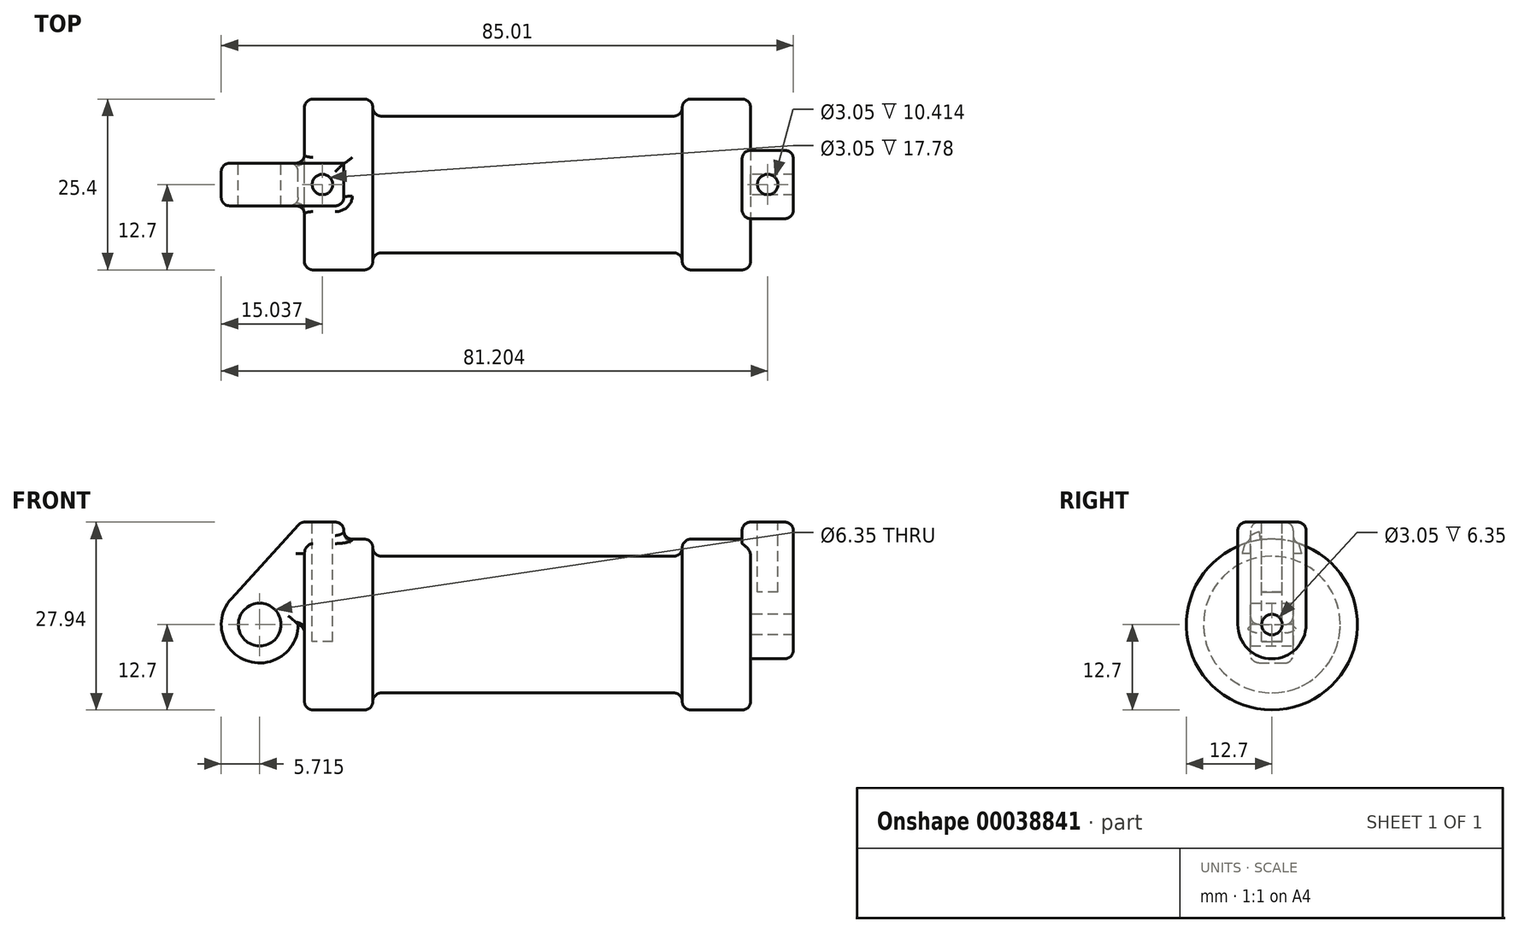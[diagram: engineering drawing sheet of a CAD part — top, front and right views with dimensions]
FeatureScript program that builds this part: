
annotation { "Feature Type Name" : "Feature", "Feature Type Description" : "" }
export const myFeature = defineFeature(function(context is Context, id is Id, definition is map)
    precondition{}
    {
        {
            var Q0;
            Q0=qCreatedBy(makeId("Front.planeOp"),FACE);
            var sketch = newSketch(context, id + "F0", { "sketchPlane" : qUnion([Q0])});
            skLineSegment(sketch, "E0", {"start": v(0, 0) * mm, "end": v(0, 12.7) * mm});
            skLineSegment(sketch, "E1", {"start": v(0, 12.7) * mm, "end": v(10.16, 12.7) * mm});
            skLineSegment(sketch, "E2", {"start": v(10.16, 12.7) * mm, "end": v(10.16, 10.16) * mm});
            skLineSegment(sketch, "E3", {"start": v(10.16, 10.16) * mm, "end": v(56.13, 10.16) * mm});
            skLineSegment(sketch, "E4", {"start": v(56.13, 10.16) * mm, "end": v(56.13, 12.7) * mm});
            skLineSegment(sketch, "E5", {"start": v(56.13, 12.7) * mm, "end": v(66.3, 12.7) * mm});
            skLineSegment(sketch, "E6", {"start": v(66.3, 12.7) * mm, "end": v(66.3, 0) * mm});
            skLineSegment(sketch, "E7", {"start": v(66.3, 0) * mm, "end": v(0, 0) * mm});
            skLineSegment(sketch, "E8", {"start": v(5.84, 15.24) * mm, "end": v(-0.5, 15.24) * mm});
            skLineSegment(sketch, "E9", {"start": v(-0.5, 15.24) * mm, "end": v(-10.88, 3.85) * mm});
            skLineSegment(sketch, "E10", {"start": v(0, 0) * mm, "end": v(-6.65, 0) * mm});
            skCircle(sketch, "E11", {"center": v(-6.65, 0) * mm, "radius": 5.72 * mm});
            skCircle(sketch, "E12", {"center": v(-6.65, 0) * mm, "radius": 3.18 * mm});
            skLineSegment(sketch, "E13", {"start": v(5.84, 15.24) * mm, "end": v(5.84, -9.4) * mm});
            skLineSegment(sketch, "E14", {"start": v(5.84, -9.4) * mm, "end": v(-8.18, -5.5) * mm});
            skSolve(sketch);
        }
        {
            var Q0;
            {var subQ6=sQuery(id+"F0.wireOp",EDGE,"E2");Q0=makeQuery(id+"F0.imprint","IMPRINT",FACE,{"disambiguationData":[TD([[makeQuery(id+"F0.imprint","IMPRINT",EDGE,{"derivedFrom":subQ6}),-1.0]])]});}
            var Q1;
            {var subQ5=sQuery(id+"F0.wireOp",EDGE,"E0");Q1=makeQuery(id+"F0.imprint","IMPRINT",FACE,{"disambiguationData":[TD([[makeQuery(id+"F0.imprint","IMPRINT",EDGE,{"derivedFrom":subQ5}),-1.0]])]});}
            var Q2;
            Q2=sQuery(id+"F0.wireOp",EDGE,"E7");
            revolve(context, id + "F1", {"entities" : qUnion([Q0, Q1]), "axis" : qUnion([Q2]), "revolveType" : RevolveType.FULL});
        }
        {
            var Q0;
            {var subQ8=sQuery(id+"F0.wireOp",EDGE,"E0");Q0=makeQuery(id+"F0.imprint","IMPRINT",FACE,{"disambiguationData":[TD([[makeQuery(id+"F0.imprint","IMPRINT",EDGE,{"derivedFrom":subQ8}),1.0]])]});}
            var Q1;
            {var subQ0=sQuery(id+"F0.wireOp",EDGE,"E12");Q1=makeQuery(id+"F0.imprint","IMPRINT",FACE,{"disambiguationData":[TD([[makeQuery(id+"F0.imprint","IMPRINT",EDGE,{"derivedFrom":subQ0}),-1.0]])]});}
            var Q2;
            {var subQ5=sQuery(id+"F0.wireOp",EDGE,"E0");Q2=makeQuery(id+"F0.imprint","IMPRINT",FACE,{"disambiguationData":[TD([[makeQuery(id+"F0.imprint","IMPRINT",EDGE,{"derivedFrom":subQ5}),-1.0]])]});}
            extrude(context, id + "F2", {"entities" : qUnion([Q0, Q1, Q2]), "operationType" : NewBodyOperationType.ADD, "endBound" : BoundingType.SYMMETRIC, "depth" : 6.35 * mm});
        }
        {
            var Q0;
            Q0=makeQuery(id+"F1.opRevolve","SWEPT_FACE",FACE,{"disambiguationData":[OSD([sQuery(id+"F0.wireOp",EDGE,"E6")])]});
            var sketch = newSketch(context, id + "F3", { "sketchPlane" : qUnion([Q0])});
            skCircle(sketch, "E15", {"center": v(0, 0) * mm, "radius": 5.08 * mm});
            skCircle(sketch, "E16", {"center": v(0, 0) * mm, "radius": 1.52 * mm});
            skLineSegment(sketch, "E17", {"start": v(-5.08, 0) * mm, "end": v(-5.08, 15.24) * mm});
            skLineSegment(sketch, "E18", {"start": v(-5.08, 15.24) * mm, "end": v(5.08, 15.24) * mm});
            skLineSegment(sketch, "E19", {"start": v(5.08, 0) * mm, "end": v(5.08, 15.28) * mm});
            skSolve(sketch);
        }
        {
            var Q0;
            Q0=makeQuery(id+"F3.imprint","IMPRINT",FACE,{"disambiguationData":[TD([[makeQuery(id+"F3.imprint","IMPRINT",EDGE,{"derivedFrom":sQuery(id+"F3.wireOp",EDGE,"E16")}),-1.0]])]});
            var Q1;
            {var subQ5=sQuery(id+"F3.wireOp",EDGE,"E18");Q1=makeQuery(id+"F3.imprint","IMPRINT",FACE,{"disambiguationData":[TD([[makeQuery(id+"F3.imprint","IMPRINT",EDGE,{"derivedFrom":subQ5}),-1.0]])]});}
            var Q2;
            {var subQ3=sQuery(id+"F3.wireOp",EDGE,"E15");var subQ5=sQuery(id+"F3.wireOp",EDGE,"E17");var subQ7=makeQuery(id+"F3.imprint","INTERSECT",VERTEX,{"derivedFrom":[subQ3,subQ5]});Q2=makeQuery(id+"F3.imprint","IMPRINT",FACE,{"disambiguationData":[TD([[makeQuery(id+"F3.imprint","IMPRINT",EDGE,{"disambiguationData":[TD([[subQ7,1.0]])],"derivedFrom":subQ3}),-1.0]])]});}
            extrude(context, id + "F4", {"entities" : qUnion([Q0, Q1, Q2]), "operationType" : NewBodyOperationType.ADD, "depth" : 6.35 * mm});
        }
        {
            var Q0;
            Q0=makeQuery(id+"F4.opExtrude","CAP_FACE",FACE,{"disambiguationData":[OSD([sQuery(id+"F3.wireOp",EDGE,"E15"),sQuery(id+"F3.wireOp",EDGE,"E16"),sQuery(id+"F3.wireOp",EDGE,"E17"),sQuery(id+"F3.wireOp",EDGE,"E18"),sQuery(id+"F3.wireOp",EDGE,"E19")])],"isStart":true});
            extrude(context, id + "F5", {"entities" : qUnion([Q0]), "operationType" : NewBodyOperationType.ADD, "depth" : 1.27 * mm});
        }
        {
            var Q0;
            {var subQ0=sQuery(id+"F3.wireOp",EDGE,"E18");Q0=makeQuery(id+"F5.boolean.opBoolean","MERGE",FACE,{"derivedFrom":[makeQuery(id+"F4.opExtrude","SWEPT_FACE",FACE,{"disambiguationData":[OSD([subQ0])]}),makeQuery(id+"F5.opExtrude","SWEPT_FACE",FACE,{"disambiguationData":[OSD([subQ0])]})]});}
            var sketch = newSketch(context, id + "F6", { "sketchPlane" : qUnion([Q0])});
            skLineSegment(sketch, "E20", {"start": v(68.83, 5.08) * mm, "end": v(68.83, -5.08) * mm, "construction": true});
            skCircle(sketch, "E21", {"center": v(68.83, 0) * mm, "radius": 1.52 * mm});
            skSolve(sketch);
        }
        {
            var Q0;
            Q0=makeQuery(id+"F6.imprint","IMPRINT",FACE,{"disambiguationData":[TD([[makeQuery(id+"F6.imprint","IMPRINT",EDGE,{"derivedFrom":sQuery(id+"F6.wireOp",EDGE,"E21")}),1.0]])]});
            extrude(context, id + "F7", {"entities" : qUnion([Q0]), "operationType" : NewBodyOperationType.REMOVE, "oppositeDirection" : true, "depth" : 10.4 * mm});
        }
        {
            var Q0;
            Q0=makeQuery(id+"F2.opExtrude","SWEPT_FACE",FACE,{"disambiguationData":[OSD([sQuery(id+"F0.wireOp",EDGE,"E8")])]});
            var sketch = newSketch(context, id + "F8", { "sketchPlane" : qUnion([Q0])});
            skLineSegment(sketch, "E22", {"start": v(2.67, 3.18) * mm, "end": v(2.67, -3.18) * mm, "construction": true});
            skCircle(sketch, "E23", {"center": v(2.67, 0) * mm, "radius": 1.52 * mm});
            skSolve(sketch);
        }
        {
            var Q0;
            Q0=makeQuery(id+"F8.imprint","IMPRINT",FACE,{"disambiguationData":[TD([[makeQuery(id+"F8.imprint","IMPRINT",EDGE,{"derivedFrom":sQuery(id+"F8.wireOp",EDGE,"E23")}),1.0]])]});
            var Q1;
            Q1=sQuery(id+"F8.wireOp",EDGE,"E23");
            extrude(context, id + "F9", {"entities" : qUnion([Q0]), "operationType" : NewBodyOperationType.REMOVE, "surfaceEntities" : qUnion([Q1]), "oppositeDirection" : true, "depth" : 17.78 * mm});
        }
        {
            var Q0;
            Q0=makeQuery(id+"F1.opRevolve","SWEPT_EDGE",EDGE,{"disambiguationData":[OSD([sQuery(id+"F0.wireOp",EDGE,"E1"),sQuery(id+"F0.wireOp",EDGE,"E2")])]});
            var Q1;
            Q1=makeQuery(id+"F1.opRevolve","SWEPT_EDGE",EDGE,{"disambiguationData":[OSD([sQuery(id+"F0.wireOp",EDGE,"E0"),sQuery(id+"F0.wireOp",EDGE,"E1")])]});
            var Q2;
            Q2=makeQuery(id+"F1.opRevolve","SWEPT_EDGE",EDGE,{"disambiguationData":[OSD([sQuery(id+"F0.wireOp",EDGE,"E3"),sQuery(id+"F0.wireOp",EDGE,"E4")])]});
            var Q3;
            Q3=makeQuery(id+"F1.opRevolve","SWEPT_EDGE",EDGE,{"disambiguationData":[OSD([sQuery(id+"F0.wireOp",EDGE,"E4"),sQuery(id+"F0.wireOp",EDGE,"E5")])]});
            var Q4;
            Q4=makeQuery(id+"F4.boolean.opBoolean","SPLIT",EDGE,{"disambiguationData":[OD(1.0)],"derivedFrom":makeQuery(id+"F1.opRevolve","SWEPT_EDGE",EDGE,{"disambiguationData":[OSD([sQuery(id+"F0.wireOp",EDGE,"E5"),sQuery(id+"F0.wireOp",EDGE,"E6")])]})});
            fillet(context, id + "F10", {"entities" : qUnion([Q0, Q1, Q2, Q3, Q4]), "radius" : 1.27 * mm, "tangentPropagation" : true, "allowEdgeOverflow" : false});
        }
        {
            var Q0;
            Q0=makeQuery(id+"F2.opExtrude","CAP_EDGE",EDGE,{"disambiguationData":[OSD([sQuery(id+"F0.wireOp",EDGE,"E9")])],"isStart":false});
            var Q1;
            Q1=makeQuery(id+"F2.opExtrude","CAP_EDGE",EDGE,{"disambiguationData":[OSD([sQuery(id+"F0.wireOp",EDGE,"E9")])],"isStart":true});
            var Q2;
            Q2=makeQuery(id+"F2.opExtrude","SWEPT_EDGE",EDGE,{"disambiguationData":[OSD([sQuery(id+"F0.wireOp",EDGE,"E8"),sQuery(id+"F0.wireOp",EDGE,"E9")])]});
            var Q3;
            Q3=makeQuery(id+"F2.opExtrude","CAP_EDGE",EDGE,{"disambiguationData":[OSD([sQuery(id+"F0.wireOp",EDGE,"E8")])],"isStart":false});
            var Q4;
            Q4=makeQuery(id+"F2.opExtrude","CAP_EDGE",EDGE,{"disambiguationData":[OSD([sQuery(id+"F0.wireOp",EDGE,"E13")])],"isStart":false});
            var Q5;
            Q5=makeQuery(id+"F2.opExtrude","CAP_EDGE",EDGE,{"disambiguationData":[OSD([sQuery(id+"F0.wireOp",EDGE,"E8")])],"isStart":true});
            var Q6;
            Q6=makeQuery(id+"F2.opExtrude","SWEPT_EDGE",EDGE,{"disambiguationData":[OSD([sQuery(id+"F0.wireOp",EDGE,"E8"),sQuery(id+"F0.wireOp",EDGE,"E13")])]});
            var Q7;
            Q7=makeQuery(id+"F2.opExtrude","CAP_EDGE",EDGE,{"disambiguationData":[OSD([sQuery(id+"F0.wireOp",EDGE,"E7"),sQuery(id+"F0.wireOp",EDGE,"E10")])],"isStart":false});
            var Q8;
            Q8=makeQuery(id+"F2.opExtrude","CAP_EDGE",EDGE,{"disambiguationData":[OSD([sQuery(id+"F0.wireOp",EDGE,"E7"),sQuery(id+"F0.wireOp",EDGE,"E10")])],"isStart":true});
            fillet(context, id + "F11", {"entities" : qUnion([Q0, Q1, Q2, Q3, Q4, Q5, Q6, Q7, Q8]), "radius" : 1.27 * mm, "tangentPropagation" : true, "allowEdgeOverflow" : false});
        }
        {
            var Q0;
            Q0=makeQuery(id+"F4.opExtrude","CAP_EDGE",EDGE,{"disambiguationData":[OSD([sQuery(id+"F3.wireOp",EDGE,"E19")])],"isStart":false});
            var Q1;
            {var subQ0=sQuery(id+"F3.wireOp",EDGE,"E18");var subQ1=sQuery(id+"F3.wireOp",EDGE,"E19");Q1=makeQuery(id+"F5.boolean.opBoolean","MERGE",EDGE,{"derivedFrom":[makeQuery(id+"F4.opExtrude","SWEPT_EDGE",EDGE,{"disambiguationData":[OSD([subQ0,subQ1])]}),makeQuery(id+"F5.opExtrude","SWEPT_EDGE",EDGE,{"disambiguationData":[OSD([subQ0,subQ1])]})]});}
            var Q2;
            Q2=makeQuery(id+"F4.opExtrude","CAP_EDGE",EDGE,{"disambiguationData":[OSD([sQuery(id+"F3.wireOp",EDGE,"E18")])],"isStart":false});
            var Q3;
            Q3=makeQuery(id+"F5.opExtrude","CAP_EDGE",EDGE,{"disambiguationData":[OSD([sQuery(id+"F3.wireOp",EDGE,"E18")])],"isStart":false});
            var Q4;
            {var subQ0=sQuery(id+"F3.wireOp",EDGE,"E17");var subQ1=sQuery(id+"F3.wireOp",EDGE,"E18");Q4=makeQuery(id+"F5.boolean.opBoolean","MERGE",EDGE,{"derivedFrom":[makeQuery(id+"F4.opExtrude","SWEPT_EDGE",EDGE,{"disambiguationData":[OSD([subQ0,subQ1])]}),makeQuery(id+"F5.opExtrude","SWEPT_EDGE",EDGE,{"disambiguationData":[OSD([subQ0,subQ1])]})]});}
            var Q5;
            Q5=makeQuery(id+"F5.opExtrude","CAP_EDGE",EDGE,{"disambiguationData":[OSD([sQuery(id+"F3.wireOp",EDGE,"E19")])],"isStart":false});
            var Q6;
            Q6=makeQuery(id+"F5.opExtrude","CAP_EDGE",EDGE,{"disambiguationData":[OSD([sQuery(id+"F3.wireOp",EDGE,"E17")])],"isStart":false});
            fillet(context, id + "F12", {"entities" : qUnion([Q0, Q1, Q2, Q3, Q4, Q5, Q6]), "radius" : 1.27 * mm, "tangentPropagation" : true, "allowEdgeOverflow" : false});
        }
        {
            var Q0;
            {var subQ0=sQuery(id+"F3.wireOp",EDGE,"E17");var subQ1=sQuery(id+"F3.wireOp",EDGE,"E15");Q0=makeQuery(id+"F4.boolean.opBoolean","SPLIT",EDGE,{"disambiguationData":[TD([makeQuery(id+"F4.opExtrude","SWEPT_FACE",FACE,{"disambiguationData":[OSD([subQ1])]})])],"derivedFrom":makeQuery(id+"F4.opExtrude","CAP_EDGE",EDGE,{"disambiguationData":[OSD([subQ0])],"isStart":true})});}
            var Q1;
            Q1=makeQuery(id+"F2.boolean.opBoolean","INTERSECT",EDGE,{"derivedFrom":[makeQuery(id+"F1.opRevolve","SWEPT_FACE",FACE,{"disambiguationData":[OSD([sQuery(id+"F0.wireOp",EDGE,"E1")])]}),makeQuery(id+"F2.opExtrude","CAP_FACE",FACE,{"disambiguationData":[OSD([sQuery(id+"F0.wireOp",EDGE,"E7"),sQuery(id+"F0.wireOp",EDGE,"E8"),sQuery(id+"F0.wireOp",EDGE,"E9"),sQuery(id+"F0.wireOp",EDGE,"E10"),sQuery(id+"F0.wireOp",EDGE,"E11"),sQuery(id+"F0.wireOp",EDGE,"E12"),sQuery(id+"F0.wireOp",EDGE,"E13")])],"isStart":false})]});
            fillet(context, id + "F13", {"entities" : qUnion([Q0, Q1]), "radius" : 1.27 * mm, "tangentPropagation" : true, "allowEdgeOverflow" : false});
        }
        {
            var Q0;
            Q0=makeQuery(id+"F1.opRevolve","SWEPT_EDGE",EDGE,{"disambiguationData":[OSD([sQuery(id+"F0.wireOp",EDGE,"E2"),sQuery(id+"F0.wireOp",EDGE,"E3")])]});
            fillet(context, id + "F14", {"entities" : qUnion([Q0]), "radius" : 1.27 * mm, "tangentPropagation" : true, "allowEdgeOverflow" : false});
        }
    });
